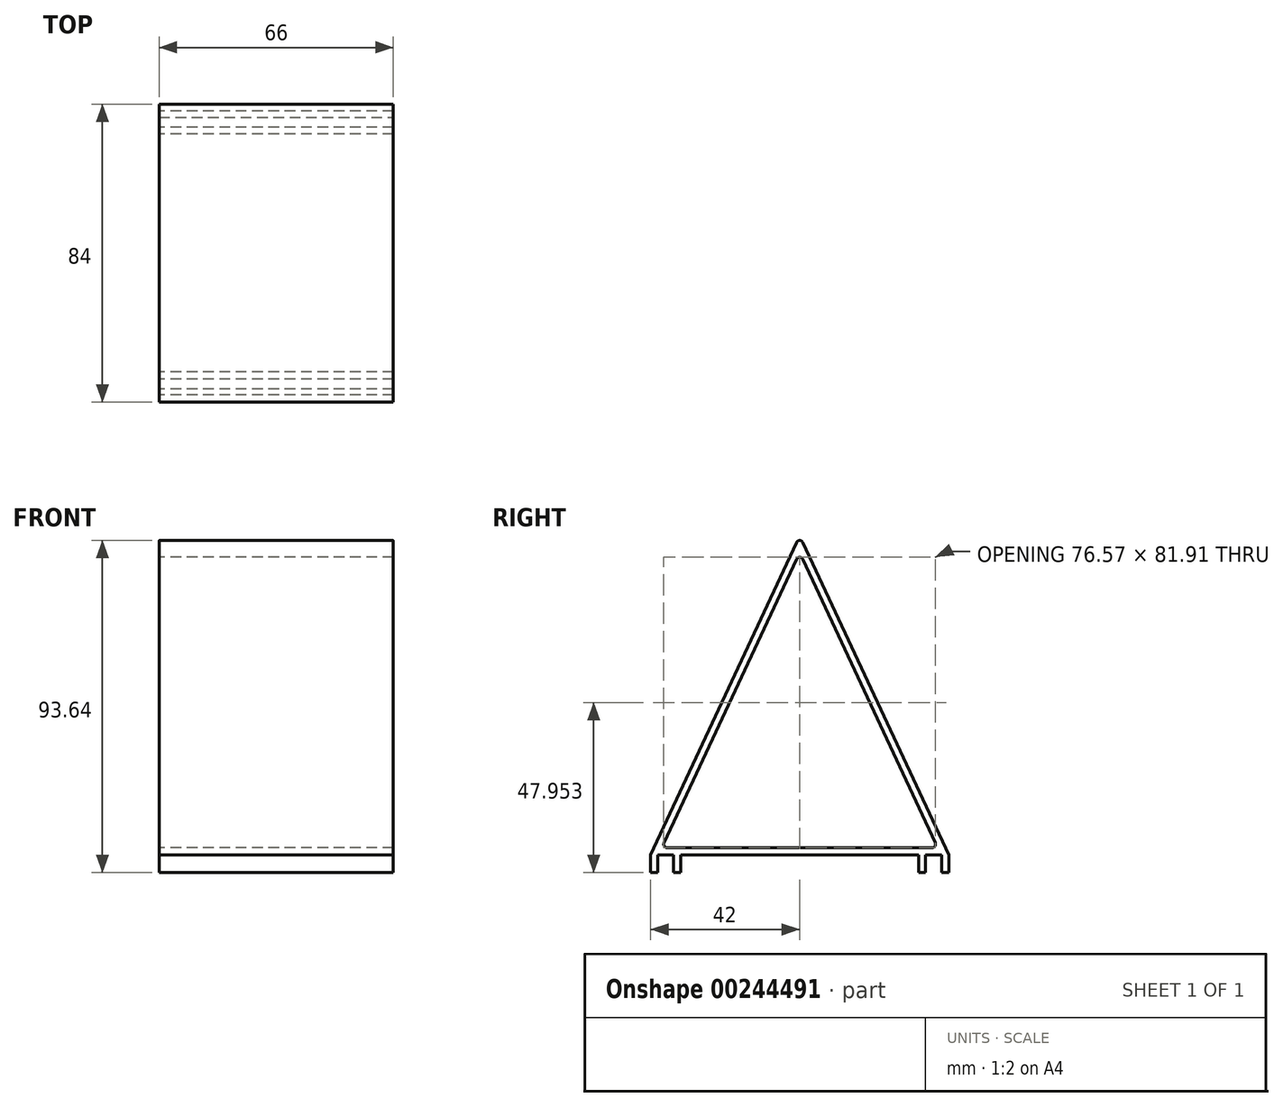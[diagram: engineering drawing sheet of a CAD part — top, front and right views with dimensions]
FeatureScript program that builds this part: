
annotation { "Feature Type Name" : "Feature", "Feature Type Description" : "" }
export const myFeature = defineFeature(function(context is Context, id is Id, definition is map)
    precondition{}
    {
        {
            var Q0;
            Q0=qCreatedBy(makeId("Right.planeOp"),FACE);
            var sketch = newSketch(context, id + "F0", { "sketchPlane" : qUnion([Q0])});
            skLineSegment(sketch, "E0", {"start": v(0, 0) * mm, "end": v(-33.5, 0) * mm});
            skLineSegment(sketch, "E1", {"start": v(-42, 0) * mm, "end": v(0, 90) * mm});
            skLineSegment(sketch, "E2", {"start": v(0, 0) * mm, "end": v(0, 90) * mm, "construction": true});
            skLineSegment(sketch, "E3.MirrorCS", {"start": v(42, 0) * mm, "end": v(0, 90) * mm});
            skLineSegment(sketch, "E4.MirrorCS", {"start": v(0, 0) * mm, "end": v(42, 0) * mm});
            skLineSegment(sketch, "E5", {"start": v(-42, 0) * mm, "end": v(-42, -5) * mm});
            skLineSegment(sketch, "E6", {"start": v(-42, -5) * mm, "end": v(-40, -5) * mm});
            skLineSegment(sketch, "E7", {"start": v(-40, -5) * mm, "end": v(-40, 0) * mm});
            skLineSegment(sketch, "E8", {"start": v(-35.5, 0) * mm, "end": v(-35.5, -5) * mm});
            skLineSegment(sketch, "E9", {"start": v(-35.5, -5) * mm, "end": v(-33.5, -5) * mm});
            skLineSegment(sketch, "E10", {"start": v(-33.5, -5) * mm, "end": v(-33.5, 0) * mm});
            skLineSegment(sketch, "E11.0", {"start": v(0, 2) * mm, "end": v(-38.86, 2) * mm});
            skLineSegment(sketch, "E12.trimOffspring", {"start": v(-35.5, 0) * mm, "end": v(-40, 0) * mm});
            skLineSegment(sketch, "E13.trimOffspring", {"start": v(-38.86, 2) * mm, "end": v(0, 85.27) * mm});
            skLineSegment(sketch, "E14.MirrorCS", {"start": v(38.86, 2) * mm, "end": v(0, 85.27) * mm});
            skLineSegment(sketch, "E15.MirrorCS", {"start": v(0, 2) * mm, "end": v(38.86, 2) * mm});
            skLineSegment(sketch, "E16.MirrorCS", {"start": v(33.5, -5) * mm, "end": v(33.5, 0) * mm});
            skLineSegment(sketch, "E17.MirrorCS", {"start": v(35.5, -5) * mm, "end": v(33.5, -5) * mm});
            skLineSegment(sketch, "E18.MirrorCS", {"start": v(35.5, 0) * mm, "end": v(35.5, -5) * mm});
            skLineSegment(sketch, "E19.MirrorCS", {"start": v(40, -5) * mm, "end": v(40, 0) * mm});
            skLineSegment(sketch, "E20.MirrorCS", {"start": v(42, -5) * mm, "end": v(40, -5) * mm});
            skLineSegment(sketch, "E21.MirrorCS", {"start": v(42, 0) * mm, "end": v(42, -5) * mm});
            skSolve(sketch);
        }
        {
            var Q0;
            Q0 = qSketchRegion(id + "F0", true);
            extrude(context, id + "F1", {"entities" : qUnion([Q0]), "depth" : 66 * mm});
        }
        {
            var Q0;
            Q0=makeQuery(id+"F1.opExtrude","SWEPT_EDGE",EDGE,{"disambiguationData":[OSD([sQuery(id+"F0.wireOp",EDGE,"E1"),sQuery(id+"F0.wireOp",EDGE,"E3.MirrorCS")])]});
            fillet(context, id + "F2", {"entities" : qUnion([Q0]), "radius" : 1 * mm, "tangentPropagation" : true, "allowEdgeOverflow" : false});
        }
        {
            var Q0;
            Q0=makeQuery(id+"F1.opExtrude","SWEPT_EDGE",EDGE,{"disambiguationData":[OSD([sQuery(id+"F0.wireOp",EDGE,"E13.trimOffspring"),sQuery(id+"F0.wireOp",EDGE,"E14.MirrorCS")])]});
            var Q1;
            Q1=makeQuery(id+"F1.opExtrude","SWEPT_EDGE",EDGE,{"disambiguationData":[OSD([sQuery(id+"F0.wireOp",EDGE,"E14.MirrorCS"),sQuery(id+"F0.wireOp",EDGE,"E15.MirrorCS")])]});
            var Q2;
            Q2=makeQuery(id+"F1.opExtrude","SWEPT_EDGE",EDGE,{"disambiguationData":[OSD([sQuery(id+"F0.wireOp",EDGE,"E11.0"),sQuery(id+"F0.wireOp",EDGE,"E13.trimOffspring")])]});
            fillet(context, id + "F3", {"entities" : qUnion([Q0, Q1, Q2]), "radius" : 1 * mm, "tangentPropagation" : true, "allowEdgeOverflow" : false});
        }
    });
